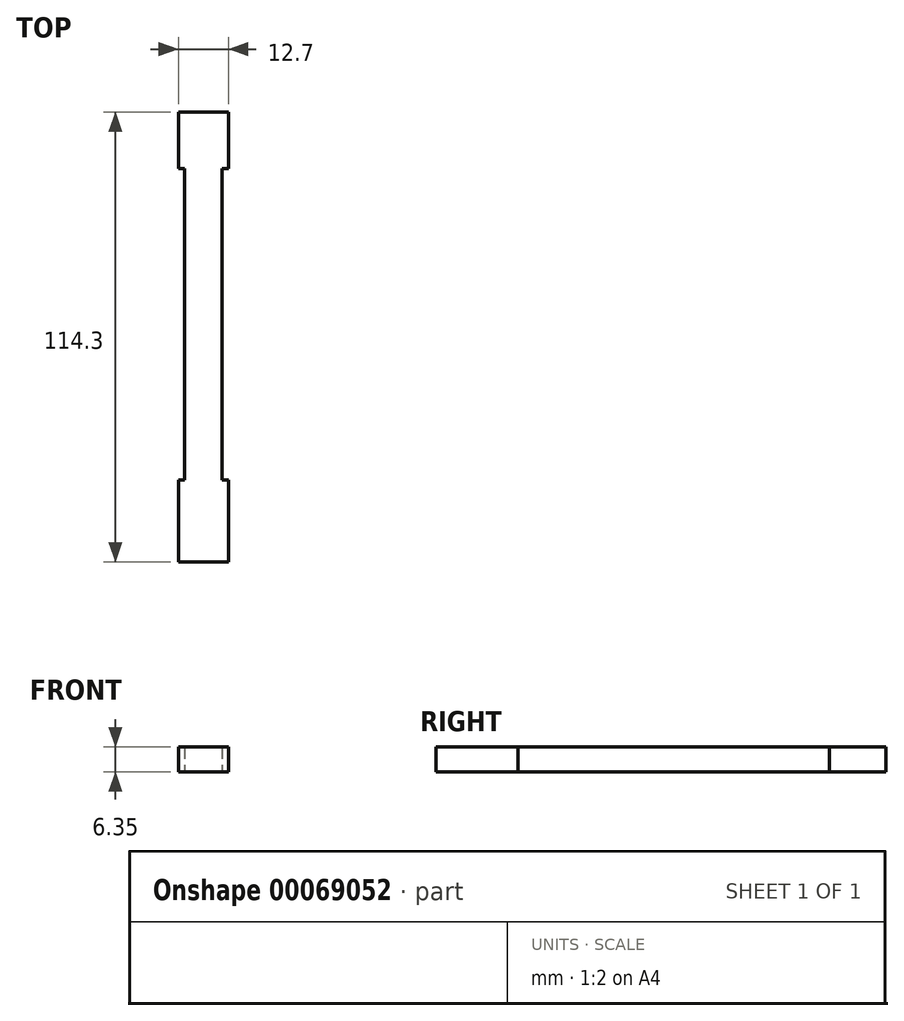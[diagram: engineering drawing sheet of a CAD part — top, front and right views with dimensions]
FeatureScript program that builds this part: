
annotation { "Feature Type Name" : "Feature", "Feature Type Description" : "" }
export const myFeature = defineFeature(function(context is Context, id is Id, definition is map)
    precondition{}
    {
        {
            var Q0;
            Q0=qCreatedBy(makeId("Top.planeOp"),FACE);
            var sketch = newSketch(context, id + "F0", { "sketchPlane" : qUnion([Q0])});
            skLineSegment(sketch, "E0", {"start": v(6.35, 57.15) * mm, "end": v(6.35, 42.75) * mm});
            skLineSegment(sketch, "E1", {"start": v(-6.35, -36.32) * mm, "end": v(-6.35, -56.31) * mm});
            skLineSegment(sketch, "E2", {"start": v(0, 57.15) * mm, "end": v(-6.35, 57.15) * mm});
            skLineSegment(sketch, "E3", {"start": v(-6.35, 57.15) * mm, "end": v(-6.35, 42.75) * mm});
            skLineSegment(sketch, "E4", {"start": v(6.35, -57.15) * mm, "end": v(6.35, -36.32) * mm});
            skLineSegment(sketch, "E5", {"start": v(0, -57.15) * mm, "end": v(6.35, -57.15) * mm});
            skLineSegment(sketch, "E6", {"start": v(4.76, 21.27) * mm, "end": v(4.76, 42.75) * mm});
            skLineSegment(sketch, "E7", {"start": v(6.35, 42.75) * mm, "end": v(4.76, 42.75) * mm});
            skLineSegment(sketch, "E8", {"start": v(-6.35, -57.15) * mm, "end": v(-6.35, -36.32) * mm});
            skLineSegment(sketch, "E9", {"start": v(6.35, -36.32) * mm, "end": v(6.35, -56.31) * mm});
            skLineSegment(sketch, "E10", {"start": v(5.51, -57.15) * mm, "end": v(0, -57.15) * mm});
            skLineSegment(sketch, "E11", {"start": v(4.76, 42.75) * mm, "end": v(4.76, -36.32) * mm});
            skLineSegment(sketch, "E12", {"start": v(4.76, -36.32) * mm, "end": v(6.35, -36.32) * mm});
            skLineSegment(sketch, "E13", {"start": v(0, 57.15) * mm, "end": v(0, -57.15) * mm});
            skLineSegment(sketch, "E14", {"start": v(0, 57.15) * mm, "end": v(6.35, 57.15) * mm});
            skLineSegment(sketch, "E15", {"start": v(-4.76, 42.75) * mm, "end": v(-4.76, -36.32) * mm});
            skLineSegment(sketch, "E16", {"start": v(-4.76, -36.32) * mm, "end": v(-6.35, -36.32) * mm});
            skLineSegment(sketch, "E17", {"start": v(0, -57.15) * mm, "end": v(-6.35, -57.15) * mm});
            skLineSegment(sketch, "E18", {"start": v(-6.35, 42.75) * mm, "end": v(-4.76, 42.75) * mm});
            skSolve(sketch);
        }
        {
            var Q0;
            Q0=makeQuery(id+"F0.imprint","IMPRINT",FACE,{"disambiguationData":[TD([[makeQuery(id+"F0.imprint","IMPRINT",EDGE,{"derivedFrom":sQuery(id+"F0.wireOp",EDGE,"E0")}),-1.0]])]});
            var Q1;
            Q1=makeQuery(id+"F0.imprint","IMPRINT",FACE,{"disambiguationData":[TD([[makeQuery(id+"F0.imprint","IMPRINT",EDGE,{"derivedFrom":sQuery(id+"F0.wireOp",EDGE,"E2")}),1.0]])]});
            extrude(context, id + "F1", {"entities" : qUnion([Q0, Q1]), "depth" : 6.35 * mm});
        }
    });
